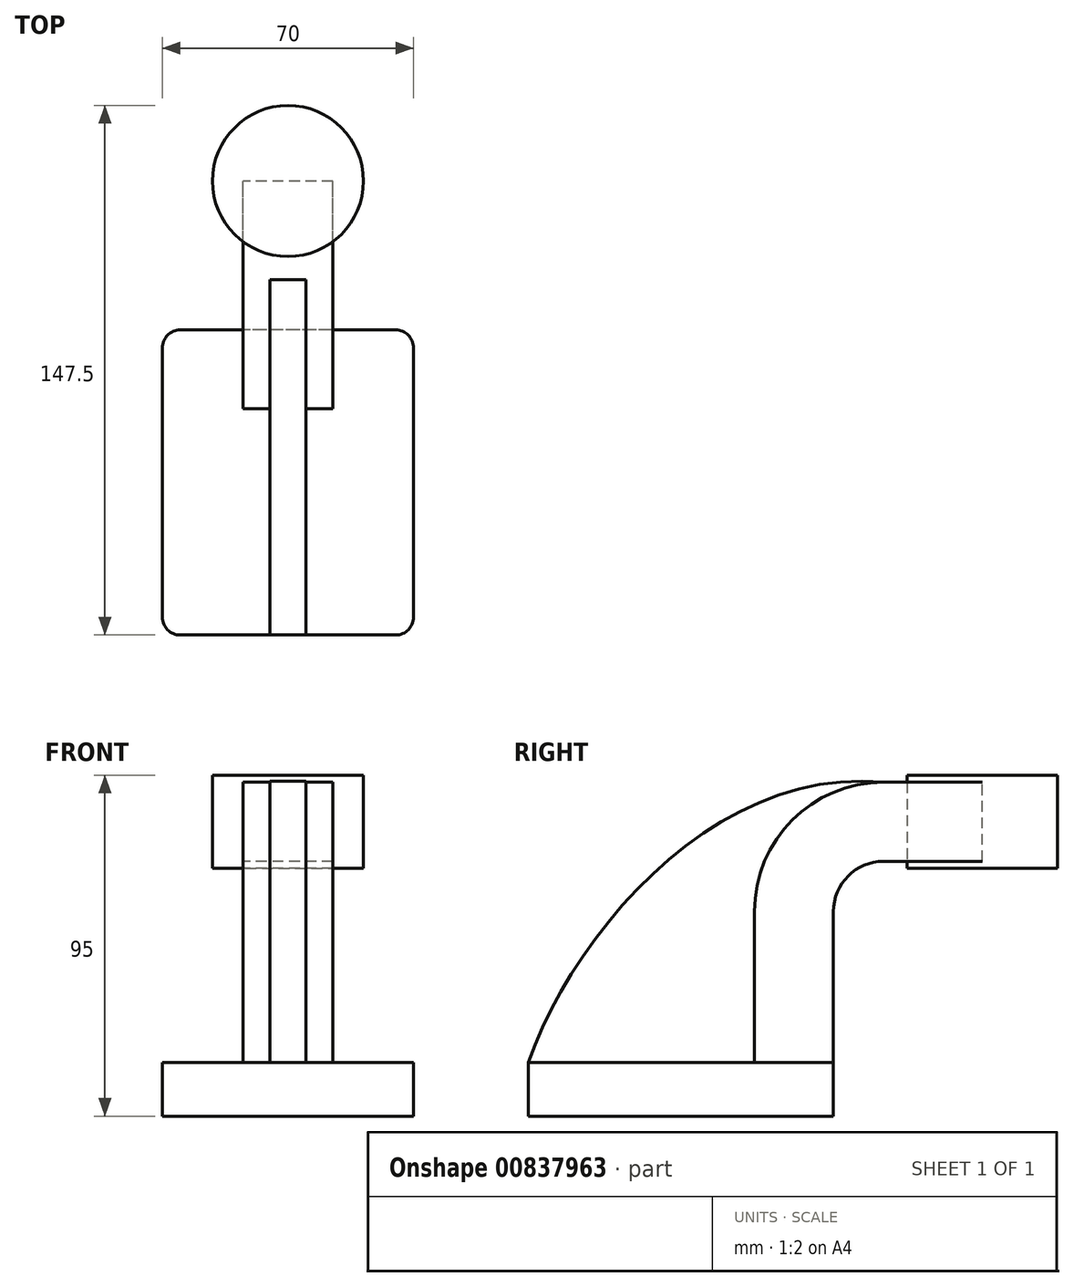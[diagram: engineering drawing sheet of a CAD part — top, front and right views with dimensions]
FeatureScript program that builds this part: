
annotation { "Feature Type Name" : "Feature", "Feature Type Description" : "" }
export const myFeature = defineFeature(function(context is Context, id is Id, definition is map)
    precondition{}
    {
        {
            var Q0;
            Q0=qCreatedBy(makeId("Right.planeOp"),FACE);
            var sketch = newSketch(context, id + "F0", { "sketchPlane" : qUnion([Q0])});
            skLineSegment(sketch, "E0.bottom", {"start": v(42.5, 7.5) * mm, "end": v(-42.5, 7.5) * mm});
            skLineSegment(sketch, "E0.top", {"start": v(42.5, -7.5) * mm, "end": v(-42.5, -7.5) * mm});
            skLineSegment(sketch, "E0.left", {"start": v(42.5, 7.5) * mm, "end": v(42.5, -7.5) * mm});
            skLineSegment(sketch, "E0.right", {"start": v(-42.5, 7.5) * mm, "end": v(-42.5, -7.5) * mm});
            skPoint(sketch, "E0.middle", {"position": v(0, 0) * mm});
            skLineSegment(sketch, "E1.bottom", {"start": v(105, 61.5) * mm, "end": v(70, 61.5) * mm});
            skLineSegment(sketch, "E1.top", {"start": v(105, 87.5) * mm, "end": v(70, 87.5) * mm});
            skLineSegment(sketch, "E1.left", {"start": v(105, 61.5) * mm, "end": v(105, 87.5) * mm});
            skLineSegment(sketch, "E1.right", {"start": v(70, 61.5) * mm, "end": v(70, 87.5) * mm});
            skPoint(sketch, "E1.middle", {"position": v(87.5, 74.5) * mm});
            skLineSegment(sketch, "E2", {"start": v(42.5, 7.5) * mm, "end": v(42.5, 49.5) * mm});
            skArc(sketch, "E3", {"start": v(56.5, 63.5) * mm, "mid": v(46.6, 59.4) * mm, "end": v(42.5, 49.5) * mm});
            skLineSegment(sketch, "E4", {"start": v(56.5, 63.5) * mm, "end": v(83.98, 63.5) * mm});
            skLineSegment(sketch, "E5.0", {"start": v(56.5, 85.5) * mm, "end": v(83.98, 85.5) * mm});
            skArc(sketch, "E5.1", {"start": v(56.5, 85.5) * mm, "mid": v(31.04, 74.96) * mm, "end": v(20.5, 49.5) * mm});
            skLineSegment(sketch, "E5.2", {"start": v(20.5, 7.5) * mm, "end": v(20.5, 49.5) * mm});
            skLineSegment(sketch, "E6", {"start": v(83.98, 61.5) * mm, "end": v(83.98, 87.5) * mm});
            skFitSpline(sketch, "E7", {"points": [v(-42.5, 7.5) * mm, v(56.5, 85.5) * mm], "startDerivative": vector(38.6, 110) * mm, "endDerivative": vector(139.86, -13.74) * mm});
            skSolve(sketch);
        }
        {
            var Q0;
            Q0=makeQuery(id+"F0.imprint","IMPRINT",FACE,{"disambiguationData":[TD([[makeQuery(id+"F0.imprint","IMPRINT",EDGE,{"derivedFrom":sQuery(id+"F0.wireOp",EDGE,"E0.top")}),-1.0]])]});
            extrude(context, id + "F1", {"entities" : qUnion([Q0]), "endBound" : BoundingType.SYMMETRIC, "depth" : 70 * mm, "offsetDistance" : 25 * mm});
        }
        {
            var Q0;
            {var subQ1=sQuery(id+"F0.wireOp",EDGE,"E2");Q0=makeQuery(id+"F0.imprint","IMPRINT",FACE,{"disambiguationData":[TD([[makeQuery(id+"F0.imprint","IMPRINT",EDGE,{"derivedFrom":subQ1}),1.0]])]});}
            var Q1;
            {var subQ0=sQuery(id+"F0.wireOp",EDGE,"E4");var subQ1=sQuery(id+"F0.wireOp",EDGE,"E1.right");var subQ2=makeQuery(id+"F0.imprint","INTERSECT",VERTEX,{"derivedFrom":[subQ1,subQ0]});Q1=makeQuery(id+"F0.imprint","IMPRINT",FACE,{"disambiguationData":[TD([[makeQuery(id+"F0.imprint","IMPRINT",EDGE,{"disambiguationData":[TD([[subQ2,-1.0]])],"derivedFrom":subQ1}),-1.0]])]});}
            extrude(context, id + "F2", {"entities" : qUnion([Q0, Q1]), "operationType" : NewBodyOperationType.ADD, "endBound" : BoundingType.SYMMETRIC, "depth" : 25 * mm, "offsetDistance" : 25 * mm});
        }
        {
            var Q0;
            Q0=makeQuery(id+"F0.imprint","IMPRINT",FACE,{"disambiguationData":[TD([[makeQuery(id+"F0.imprint","IMPRINT",EDGE,{"derivedFrom":sQuery(id+"F0.wireOp",EDGE,"E5.1")}),-1.0]])]});
            extrude(context, id + "F3", {"entities" : qUnion([Q0]), "operationType" : NewBodyOperationType.ADD, "endBound" : BoundingType.SYMMETRIC, "depth" : 10 * mm, "offsetDistance" : 25 * mm});
        }
        {
            var Q0;
            {var subQ4=sQuery(id+"F0.wireOp",EDGE,"E1.left");Q0=makeQuery(id+"F0.imprint","IMPRINT",FACE,{"disambiguationData":[TD([[makeQuery(id+"F0.imprint","IMPRINT",EDGE,{"derivedFrom":subQ4}),1.0]])]});}
            var Q1;
            Q1=sQuery(id+"F0.wireOp",EDGE,"E6");
            revolve(context, id + "F4", {"surfaceOperationType" : NewSurfaceOperationType.NEW, "entities" : qUnion([Q0]), "axis" : qUnion([Q1]), "revolveType" : RevolveType.FULL});
        }
        {
            var Q0;
            Q0=makeQuery(id+"F1.opExtrude","CAP_EDGE",EDGE,{"disambiguationData":[OSD([sQuery(id+"F0.wireOp",EDGE,"E0.left")])],"isStart":false});
            var Q1;
            Q1=makeQuery(id+"F1.opExtrude","CAP_EDGE",EDGE,{"disambiguationData":[OSD([sQuery(id+"F0.wireOp",EDGE,"E0.left")])],"isStart":true});
            var Q2;
            Q2=makeQuery(id+"F1.opExtrude","CAP_EDGE",EDGE,{"disambiguationData":[OSD([sQuery(id+"F0.wireOp",EDGE,"E0.right")])],"isStart":false});
            var Q3;
            Q3=makeQuery(id+"F1.opExtrude","CAP_EDGE",EDGE,{"disambiguationData":[OSD([sQuery(id+"F0.wireOp",EDGE,"E0.right")])],"isStart":true});
            fillet(context, id + "F5", {"entities" : qUnion([Q0, Q1, Q2, Q3]), "radius" : 5 * mm, "tangentPropagation" : true, "allowEdgeOverflow" : false});
        }
    });
